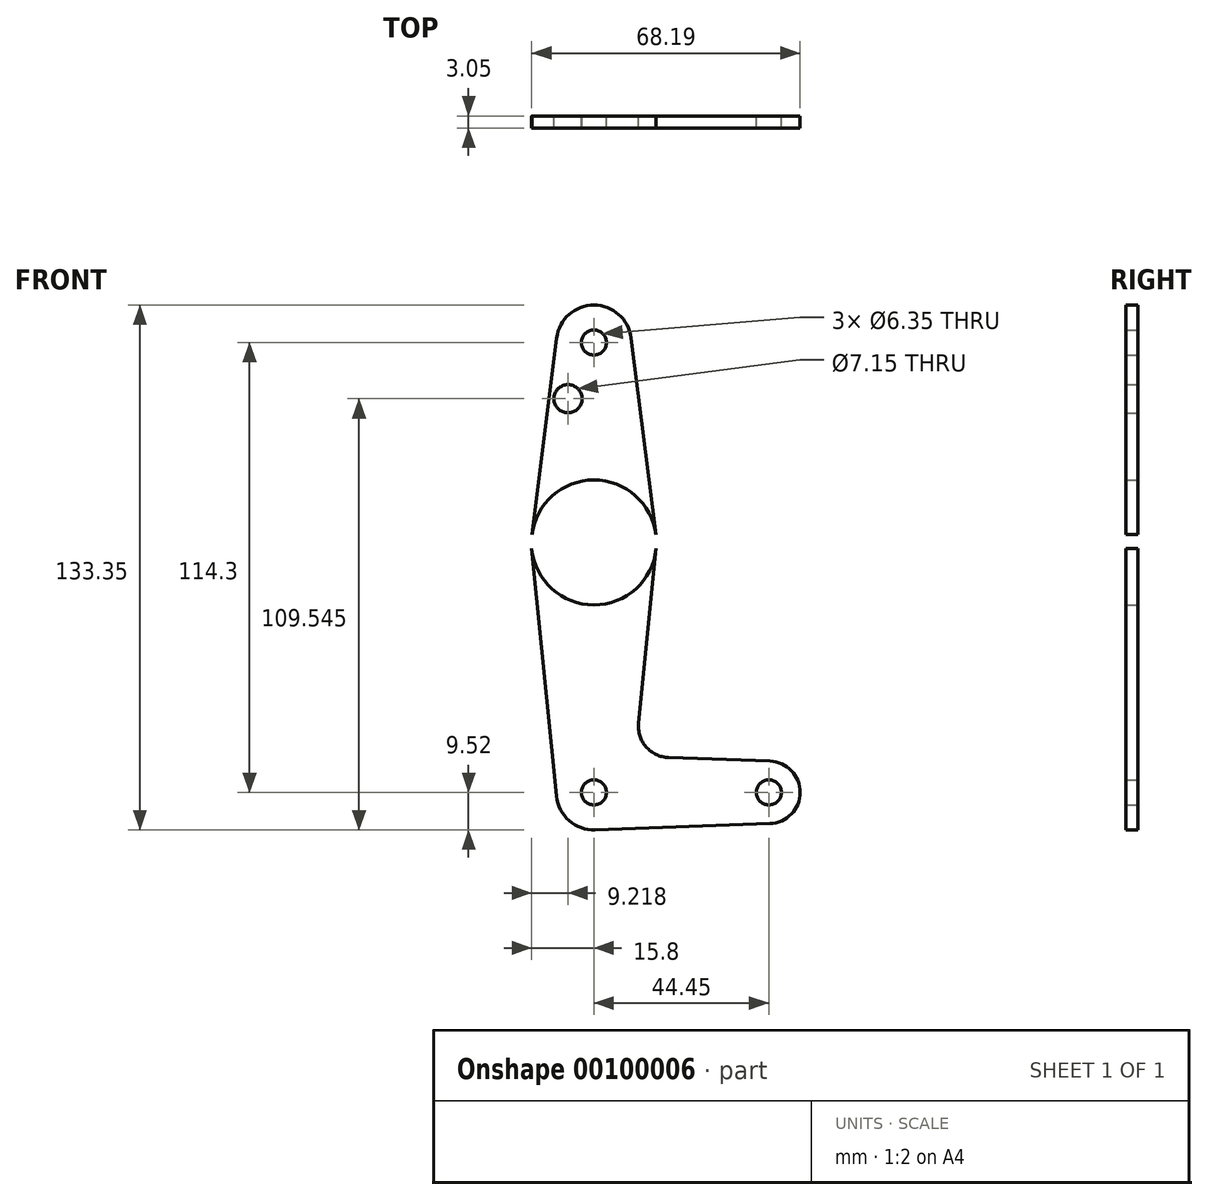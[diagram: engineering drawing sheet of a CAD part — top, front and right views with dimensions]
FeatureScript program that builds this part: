
annotation { "Feature Type Name" : "Feature", "Feature Type Description" : "" }
export const myFeature = defineFeature(function(context is Context, id is Id, definition is map)
    precondition{}
    {
        {
            var Q0;
            Q0=qCreatedBy(makeId("Front.planeOp"),FACE);
            var sketch = newSketch(context, id + "F0", { "sketchPlane" : qUnion([Q0])});
            skLineSegment(sketch, "E0", {"start": v(0, 114.3) * mm, "end": v(0, 0) * mm});
            skLineSegment(sketch, "E1", {"start": v(0, 0) * mm, "end": v(44.45, 0) * mm});
            skCircle(sketch, "E2", {"center": v(0, 114.3) * mm, "radius": 9.53 * mm});
            skCircle(sketch, "E3", {"center": v(0, 63.5) * mm, "radius": 15.88 * mm});
            skCircle(sketch, "E4", {"center": v(0, 0) * mm, "radius": 9.53 * mm});
            skCircle(sketch, "E5", {"center": v(44.45, 0) * mm, "radius": 7.94 * mm});
            skLineSegment(sketch, "E6", {"start": v(9.45, 115.5) * mm, "end": v(15.75, 65.48) * mm});
            skLineSegment(sketch, "E7", {"start": v(-9.45, 115.5) * mm, "end": v(-15.75, 65.48) * mm});
            skLineSegment(sketch, "E8", {"start": v(15.8, 61.91) * mm, "end": v(11.34, 17.6) * mm});
            skLineSegment(sketch, "E9", {"start": v(-15.8, 61.91) * mm, "end": v(-9.48, -0.95) * mm});
            skCircle(sketch, "E10", {"center": v(-6.58, 100.03) * mm, "radius": 3.58 * mm});
            skCircle(sketch, "E11", {"center": v(0, 114.3) * mm, "radius": 3.18 * mm});
            skCircle(sketch, "E12", {"center": v(0, 63.5) * mm, "radius": 3.18 * mm});
            skCircle(sketch, "E13", {"center": v(0, 0) * mm, "radius": 3.18 * mm});
            skCircle(sketch, "E14", {"center": v(44.45, 0) * mm, "radius": 3.18 * mm});
            skLineSegment(sketch, "E15", {"start": v(0.34, -9.52) * mm, "end": v(44.73, -7.93) * mm});
            skLineSegment(sketch, "E16", {"start": v(18.97, 8.85) * mm, "end": v(44.73, 7.93) * mm});
            skArc(sketch, "E17.filletArc", {"start": v(11.34, 17.6) * mm, "mid": v(13.26, 11.57) * mm, "end": v(18.97, 8.85) * mm});
            skSolve(sketch);
        }
        {
            var Q0;
            {var subQ5=sQuery(id+"F0.wireOp",EDGE,"E6");Q0=makeQuery(id+"F0.imprint","IMPRINT",FACE,{"disambiguationData":[TD([[makeQuery(id+"F0.imprint","IMPRINT",EDGE,{"derivedFrom":subQ5}),-1.0]])]});}
            var Q1;
            {var subQ5=sQuery(id+"F0.wireOp",EDGE,"E9");Q1=makeQuery(id+"F0.imprint","IMPRINT",FACE,{"disambiguationData":[TD([[makeQuery(id+"F0.imprint","IMPRINT",EDGE,{"derivedFrom":subQ5}),1.0]])]});}
            var Q2;
            {var subQ5=sQuery(id+"F0.wireOp",EDGE,"E15");Q2=makeQuery(id+"F0.imprint","IMPRINT",FACE,{"disambiguationData":[TD([[makeQuery(id+"F0.imprint","IMPRINT",EDGE,{"derivedFrom":subQ5}),1.0]])]});}
            var Q3;
            Q3=makeQuery(id+"F0.imprint","IMPRINT",FACE,{"disambiguationData":[TD([[makeQuery(id+"F0.imprint","IMPRINT",EDGE,{"derivedFrom":sQuery(id+"F0.wireOp",EDGE,"E11")}),-1.0]])]});
            var Q4;
            Q4=makeQuery(id+"F0.imprint","IMPRINT",FACE,{"disambiguationData":[TD([[makeQuery(id+"F0.imprint","IMPRINT",EDGE,{"derivedFrom":sQuery(id+"F0.wireOp",EDGE,"E14")}),-1.0]])]});
            var Q5;
            {var subQ0=sQuery(id+"F0.wireOp",EDGE,"E3");var subQ2=sQuery(id+"F0.wireOp",EDGE,"E0");var subQ3=makeQuery(id+"F0.imprint","INTERSECT",VERTEX,{"disambiguationData":[OD(0.0)],"derivedFrom":[subQ2,subQ0]});Q5=makeQuery(id+"F0.imprint","IMPRINT",FACE,{"disambiguationData":[TD([[makeQuery(id+"F0.imprint","IMPRINT",EDGE,{"disambiguationData":[TD([[subQ3,-1.0]])],"derivedFrom":subQ2}),1.0]])]});}
            var Q6;
            {var subQ0=sQuery(id+"F0.wireOp",EDGE,"E3");var subQ3=sQuery(id+"F0.wireOp",EDGE,"E0");var subQ4=makeQuery(id+"F0.imprint","INTERSECT",VERTEX,{"disambiguationData":[OD(0.0)],"derivedFrom":[subQ3,subQ0]});Q6=makeQuery(id+"F0.imprint","IMPRINT",FACE,{"disambiguationData":[TD([[makeQuery(id+"F0.imprint","IMPRINT",EDGE,{"disambiguationData":[TD([[subQ4,-1.0]])],"derivedFrom":subQ3}),-1.0]])]});}
            var Q7;
            {var subQ3=sQuery(id+"F0.wireOp",EDGE,"E4");var subQ7=sQuery(id+"F0.wireOp",EDGE,"E0");var subQ8=makeQuery(id+"F0.imprint","INTERSECT",VERTEX,{"derivedFrom":[subQ7,subQ3]});Q7=makeQuery(id+"F0.imprint","IMPRINT",FACE,{"disambiguationData":[TD([[makeQuery(id+"F0.imprint","IMPRINT",EDGE,{"disambiguationData":[TD([[subQ8,-1.0]])],"derivedFrom":subQ7}),-1.0]])]});}
            var Q8;
            {var subQ0=sQuery(id+"F0.wireOp",EDGE,"E8");Q8=makeQuery(id+"F0.imprint","IMPRINT",FACE,{"disambiguationData":[TD([[makeQuery(id+"F0.imprint","IMPRINT",EDGE,{"derivedFrom":subQ0}),-1.0]])]});}
            var Q9;
            {var subQ0=sQuery(id+"F0.wireOp",EDGE,"E7");Q9=makeQuery(id+"F0.imprint","IMPRINT",FACE,{"disambiguationData":[TD([[makeQuery(id+"F0.imprint","IMPRINT",EDGE,{"derivedFrom":subQ0}),1.0]])]});}
            var Q10;
            {var subQ0=sQuery(id+"F0.wireOp",EDGE,"E4");var subQ1=sQuery(id+"F0.wireOp",EDGE,"E0");var subQ2=makeQuery(id+"F0.imprint","INTERSECT",VERTEX,{"derivedFrom":[subQ1,subQ0]});Q10=makeQuery(id+"F0.imprint","IMPRINT",FACE,{"disambiguationData":[TD([[makeQuery(id+"F0.imprint","IMPRINT",EDGE,{"disambiguationData":[TD([[subQ2,-1.0]])],"derivedFrom":subQ1}),1.0]])]});}
            extrude(context, id + "F1", {"entities" : qUnion([Q0, Q1, Q2, Q3, Q4, Q5, Q6, Q7, Q8, Q9, Q10]), "depth" : 3.05 * mm});
        }
    });
